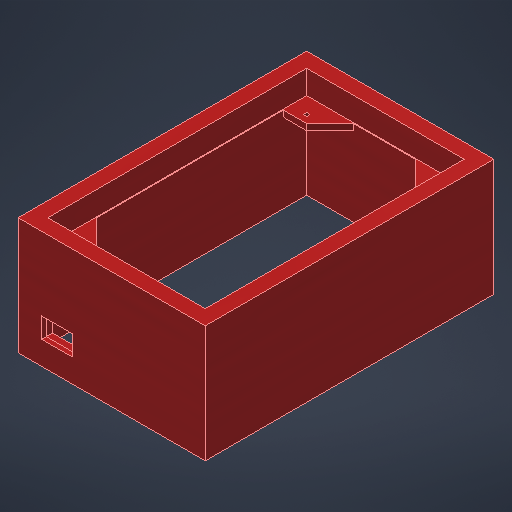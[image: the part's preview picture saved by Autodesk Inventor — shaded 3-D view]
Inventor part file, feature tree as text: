
AUTODESK INVENTOR PART (.ipt)
format: ipt  version: 2025.2 (Build 292293000, 293)  size: 305,152 bytes
history: native  units: in
note: dims shown in document units (in); Inventor stores cm internally (conversion verified against a paired STEP export)
features: extrude x9, sketch x4, plane x1
ambient origin geometry x8: Origin, YZ Plane, XZ Plane, XY Plane, X Axis, Y Axis, Z Axis, Center Point
bodies: Solid1 (feature_tree)
feature tree (14):
  extrude  "Extrusion1"  Depth=6.4961in
  plane  "Work Plane2"
  extrude  "Extrusion3"  Depth=7.2835in
  extrude  "Extrusion5"  [1 undecoded]
  extrude  "Extrusion8"  Depth=0.2756in
  extrude  "Extrusion9"  Depth=0.1575in TaperAngle=0.0deg
  extrude  "Extrusion10"  Depth=0.2756in
  extrude  "Extrusion11"  Depth=0.1575in TaperAngle=0.0deg
  extrude  "Extrusion12"  Depth=0.2756in
  extrude  "Extrusion13"  Depth=0.3937in
  sketch  "Sketch11"  dims[d0=3.937in d1=6.4961in]
  sketch  "Sketch15"  dims[d2=4.7244in d3=7.2835in]
  sketch  "Sketch16"  dims[d4=2.9528in d5=0.0in d8=-0.5984in]
  sketch  "Sketch18"  dims[d9=1.1811in d10=1.1811in d11=0.1575in d12=0.0in d17=0.1024in d18=0.1575in d19=0.0in d20=1.1811in d21=0.3937in d22=0.3937in d23=0.1024in d24=0.3937in d25=0.3937in d26=0.1024in d27=0.3937in d28=0.3937in d29=0.1024in d38=4.3307in d39=6.8898in d40=0.1969in d41=0.0in d42=0.0591in d43=0.0591in d44=0.0591in d45=0.0591in d46=0.1969in d47=0.0in d48=0.3937in d49=0.3937in d50=1.1811in d51=3.9764in d52=6.5354in d53=0.5984in d54=0.0in d56=0.5906in d57=0.5906in d58=0.5906in d59=0.1575in d60=0.0in d61=0.5906in d62=0.5906in d63=0.7717in d64=0.5118in d65=0.3937in d66=0.0in d67=0.1181in d68=0.1181in d69=0.1181in d70=0.1181in d71=0.2756in d72=0.0in]
note: 1 required parameter value undecoded (feature->parameter linkage not recoverable at this tier; creation-order binding heuristic only, values carry confidence <= 0.55)
